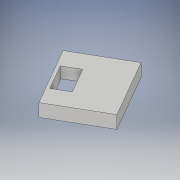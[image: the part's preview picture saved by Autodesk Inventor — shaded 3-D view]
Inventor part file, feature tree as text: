
AUTODESK INVENTOR PART (.ipt)
format: ipt  version: 2017 (Build 210142000, 142)  size: 136,192 bytes
history: native  units: in
note: dims shown in document units (in); Inventor stores cm internally (conversion verified against a paired STEP export)
features: extrude x1, sketch x1, projected_geometry x1, imported_body x1
ambient origin geometry x8: Origin, YZ Plane, XZ Plane, XY Plane, X Axis, Y Axis, Z Axis, Center Point
bodies: Solid1 (feature_tree)
feature tree (4):
  extrude  "Extrusion1"  Depth=0.3937in TaperAngle=0.0deg
  sketch  "Sketch1"  dims[d0=1.25in d1=0.3937in d2=0.0in]
  projected_geometry  "Projected Loop1"
  imported_body  "Base1"
